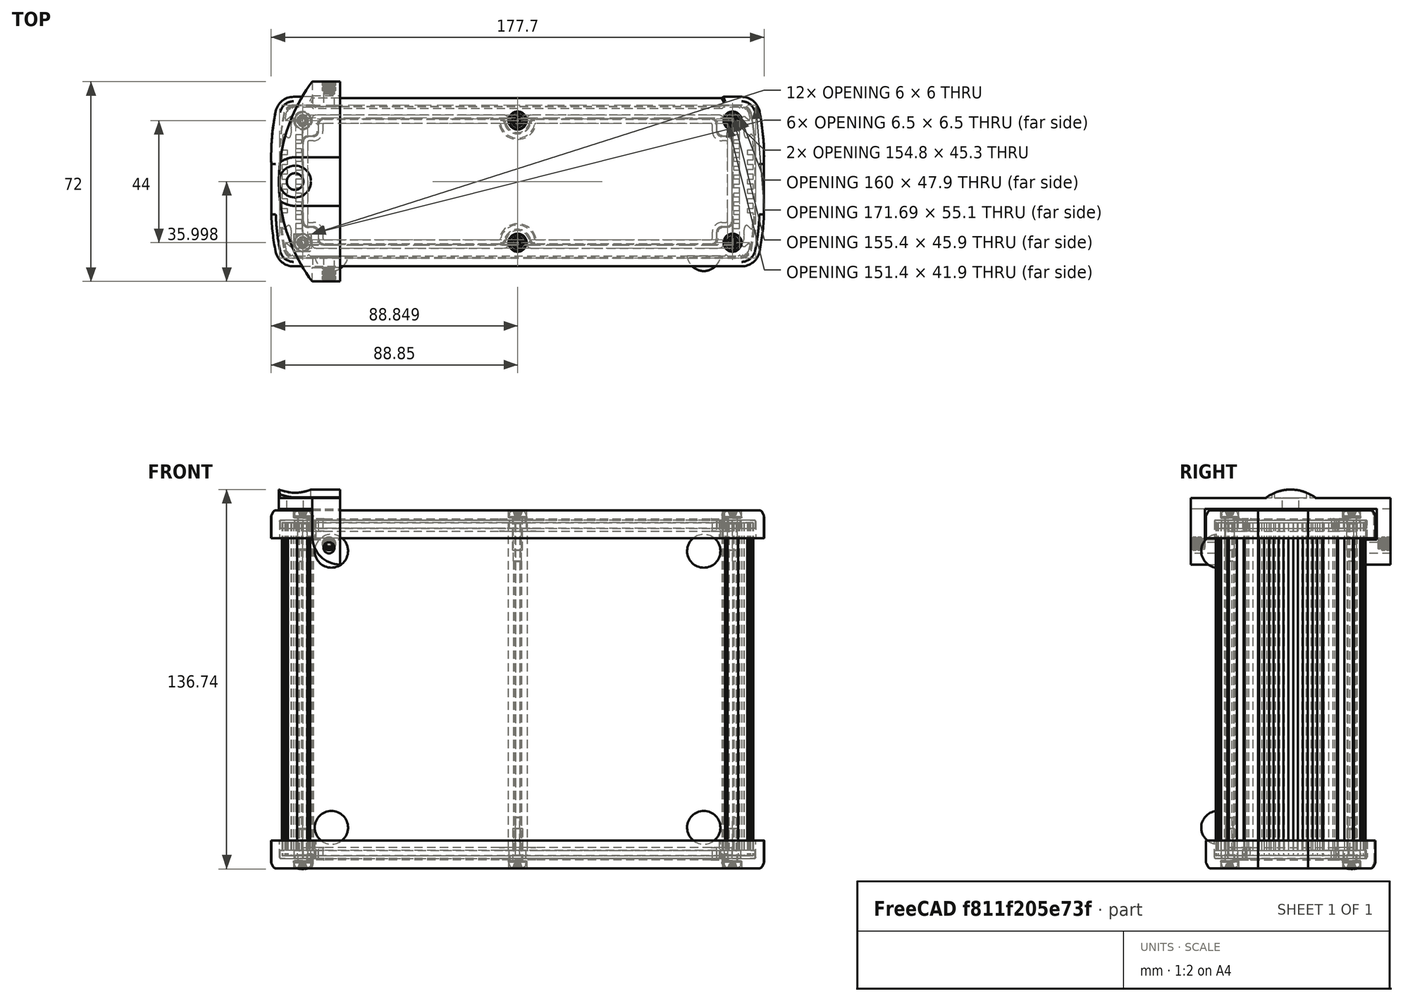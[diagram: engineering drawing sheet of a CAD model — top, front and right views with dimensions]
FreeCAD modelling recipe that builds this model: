
FCSTD DOCUMENT  (FreeCAD 0.20R29177 (Git))
Label: antennaHolder2022_07_15
License: All rights reserved
LicenseURL: http://en.wikipedia.org/wiki/All_rights_reserved
objects: Part::Cylinder×10, Part::Box×5, Part::MultiFuse×5, Part::Feature×3, Part::Cut×3, Part::MultiCommon×2
note: 28 computed .brp shape members not serialized (recipe doc carries the construction recipe); baked Part::Feature solids carry a one-line shape summary decoded from their .brp

FEATURE [Part::Feature] Feature  label="EX-64-002"
  Placement = pos=(74,0,0) rot=(0,0,1;0rad)
  shape: bbox 178.8 x 63.35 x 129.6 mm, 1628 faces, 33 solids (baked)
FEATURE [Part::Box] Box  label="out"
  AttacherType = Attacher::AttachEngine3D
  Height = 24
  Length = 10
  Placement = pos=(0,-36,45) rot=(0,0,1;0rad)
  Width = 72
FEATURE [Part::Box] Box001  label="in"
  AttacherType = Attacher::AttachEngine3D
  Height = 11
  Length = 10
  Placement = pos=(0,-31,54) rot=(0,0,1;0rad)
  Width = 62
FEATURE [Part::Box] Box002  label="in001"
  AttacherType = Attacher::AttachEngine3D
  Height = 11
  Length = 10
  Placement = pos=(0,-27,45) rot=(0,0,1;0rad)
  Width = 54
FEATURE [Part::MultiFuse] Fusion  label="in002"
  Shapes = -> [Box001,Box002]
FEATURE [Part::Cut] Cut
  Base = -> Box
  Tool = -> Fusion
FEATURE [Part::Feature] Solid  label="m3HeatSetInsert"
  Placement = pos=(6,31.5,52.5) rot=(0,0,1;0rad)
  shape: bbox 4.772 x 4.354 x 4.772 mm, 239 faces (baked)
FEATURE [Part::Cylinder] Cylinder
  Angle = 90
  AttacherType = Attacher::AttachEngine3D
  FirstAngle = 0
  Height = 5
  Placement = pos=(10,31,55) rot=(0.57735,-0.57735,-0.57735;4.18879rad)
  Radius = 10
  SecondAngle = 0
FEATURE [Part::Feature] Solid001  label="m3HeatSetInsert001"
  Placement = pos=(6,-31,52.5) rot=(0,0,1;3.14159rad)
  shape: bbox 4.772 x 4.354 x 4.772 mm, 239 faces (baked)
FEATURE [Part::Cylinder] Cylinder001
  Angle = 90
  AttacherType = Attacher::AttachEngine3D
  FirstAngle = 0
  Height = 5
  Placement = pos=(10,-31,55) rot=(0,0.707107,-0.707107;3.14159rad)
  Radius = 10
  SecondAngle = 0
FEATURE [Part::MultiFuse] Fusion001  label="out001"
  Shapes = -> [Cylinder,Cylinder001,Cut]
FEATURE [Part::Cylinder] Cylinder002
  Angle = 360
  AttacherType = Attacher::AttachEngine3D
  FirstAngle = 0
  Height = 4
  Placement = pos=(48,0,65) rot=(0,0,1;0rad)
  Radius = 60.06
  SecondAngle = 0
FEATURE [Part::Cylinder] Cylinder014  label="antennaIn001"
  Angle = 360
  AttacherType = Attacher::AttachEngine3D
  FirstAngle = 0
  Height = 10
  Placement = pos=(-6.23,0,69) rot=(0,0,1;0rad)
  Radius = 5.75
  SecondAngle = 0
FEATURE [Part::Cylinder] Cylinder013  label="antennaIn"
  Angle = 360
  AttacherType = Attacher::AttachEngine3D
  FirstAngle = 0
  Height = 10
  Placement = pos=(-6.23,0,65) rot=(0,0,1;0rad)
  Radius = 3
  SecondAngle = 0
FEATURE [Part::Cylinder] Cylinder015  label="antennaOut001"
  Angle = 360
  AttacherType = Attacher::AttachEngine3D
  FirstAngle = 0
  Height = 3
  Placement = pos=(-6.23,0,69) rot=(0,0,1;0rad)
  Radius = 8.75
  SecondAngle = 0
FEATURE [Part::Box] Box003  label="Cube"
  AttacherType = Attacher::AttachEngine3D
  Height = 3
  Length = 16.25
  Placement = pos=(-6.23,-8.75,69) rot=(0,0,1;0rad)
  Width = 17.5
FEATURE [Part::MultiFuse] Fusion002
  Shapes = -> [Fusion001,Cylinder002,Cylinder015,Box003]
FEATURE [Part::MultiFuse] Fusion003
  Shapes = -> [Cylinder013,Cylinder014]
FEATURE [Part::Cut] Cut001  label="base"
  Base = -> Fusion002
  Tool = -> Fusion003
FEATURE [Part::Cylinder] Cylinder016  label="m3HeastSetCut"
  Angle = 360
  AttacherType = Attacher::AttachEngine3D
  FirstAngle = 0
  Height = 94
  Placement = pos=(6,-47.35,51) rot=(-1,0,0;1.5708rad)
  Radius = 2
  SecondAngle = 0
FEATURE [Part::Cut] Cut002
  Base = -> Cut001
  Tool = -> Cylinder016
FEATURE [Part::Cylinder] Cylinder017  label="include001"
  Angle = 90
  AttacherType = Attacher::AttachEngine3D
  FirstAngle = 0
  Height = 87
  Placement = pos=(10,-40.75,55) rot=(0.57735,-0.57735,-0.57735;4.18879rad)
  Radius = 10
  SecondAngle = 0
FEATURE [Part::Box] Box004  label="include"
  AttacherType = Attacher::AttachEngine3D
  Height = 14
  Length = 25
  Placement = pos=(-15,-36,55) rot=(0,0,1;0rad)
  Width = 72
FEATURE [Part::Cylinder] Cylinder018
  Angle = 360
  AttacherType = Attacher::AttachEngine3D
  FirstAngle = 0
  Height = 30
  Placement = pos=(-20,0,57) rot=(0.57735,0.57735,0.57735;2.0944rad)
  Radius = 15
  SecondAngle = 0
FEATURE [Part::MultiFuse] Fusion004  label="include002"
  Shapes = -> [Cylinder017,Box004,Cylinder018]
FEATURE [Part::MultiCommon] Common
  Shapes = -> [Fusion004,Cut002]
FEATURE [Part::Cylinder] Cylinder019
  Angle = 360
  AttacherType = Attacher::AttachEngine3D
  FirstAngle = 0
  Height = 44
  Placement = pos=(48,0,35.9) rot=(0,0,1;0rad)
  Radius = 60.06
  SecondAngle = 0
FEATURE [Part::MultiCommon] Common001
  Shapes = -> [Common,Cylinder019]
